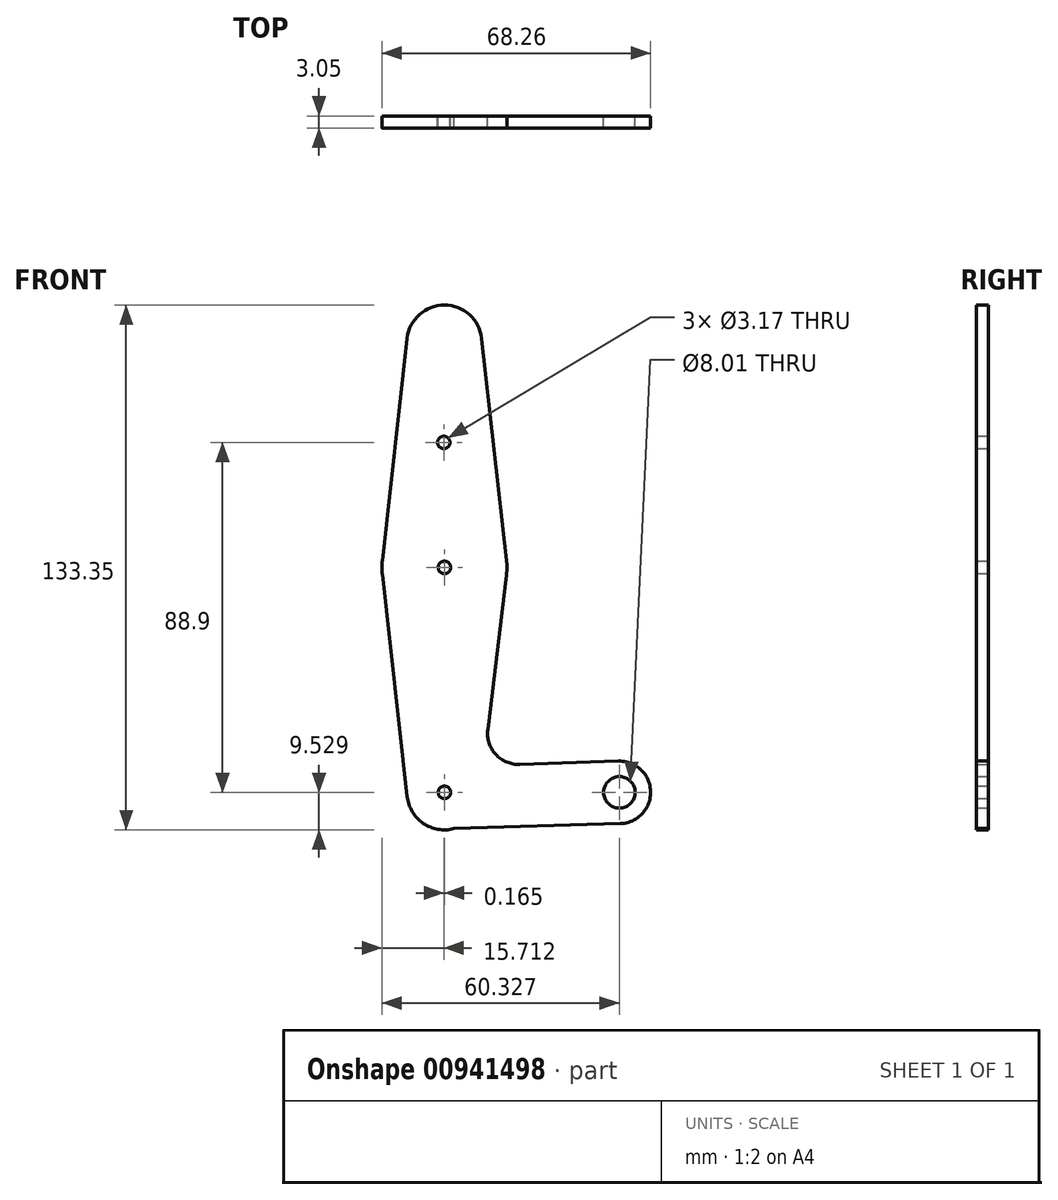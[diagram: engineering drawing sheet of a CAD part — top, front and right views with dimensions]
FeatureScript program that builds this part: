
annotation { "Feature Type Name" : "Feature", "Feature Type Description" : "" }
export const myFeature = defineFeature(function(context is Context, id is Id, definition is map)
    precondition{}
    {
        {
            var Q0;
            Q0=qCreatedBy(makeId("Front.planeOp"),FACE);
            var sketch = newSketch(context, id + "F0", { "sketchPlane" : qUnion([Q0])});
            skLineSegment(sketch, "E0", {"start": v(-39.9, 67.03) * mm, "end": v(-39.9, -47.27) * mm, "construction": true});
            skLineSegment(sketch, "E1", {"start": v(-39.9, -47.27) * mm, "end": v(4.56, -47.27) * mm, "construction": true});
            skCircle(sketch, "E2", {"center": v(-39.9, 67.03) * mm, "radius": 9.53 * mm});
            skCircle(sketch, "E3", {"center": v(-39.9, 9.88) * mm, "radius": 15.88 * mm});
            skCircle(sketch, "E4", {"center": v(-39.9, -47.27) * mm, "radius": 9.53 * mm});
            skCircle(sketch, "E5", {"center": v(4.56, -47.27) * mm, "radius": 7.94 * mm});
            skLineSegment(sketch, "E6", {"start": v(-30.43, 68.09) * mm, "end": v(-24.12, 11.64) * mm});
            skLineSegment(sketch, "E7", {"start": v(-49.36, 68.09) * mm, "end": v(-55.67, 11.64) * mm});
            skLineSegment(sketch, "E8", {"start": v(-55.67, 8.11) * mm, "end": v(-49.36, -48.33) * mm});
            skLineSegment(sketch, "E9", {"start": v(-28.88, -31.29) * mm, "end": v(-24.12, 8.1) * mm});
            skLineSegment(sketch, "E10", {"start": v(-20.71, -40.19) * mm, "end": v(4.56, -39.33) * mm});
            skCircle(sketch, "E11", {"center": v(-40.06, 41.63) * mm, "radius": 1.59 * mm});
            skCircle(sketch, "E12", {"center": v(-39.9, 9.88) * mm, "radius": 1.59 * mm});
            skCircle(sketch, "E13", {"center": v(-39.9, -47.27) * mm, "radius": 1.59 * mm});
            skCircle(sketch, "E14", {"center": v(4.56, -47.27) * mm, "radius": 4 * mm});
            skLineSegment(sketch, "E15", {"start": v(-41.75, -56.61) * mm, "end": v(4.8, -55.2) * mm});
            skPoint(sketch, "E16.newPointA", {"position": v(-30.94, -48.33) * mm});
            skPoint(sketch, "E16.newPointB", {"position": v(-39.9, -40.84) * mm});
            skArc(sketch, "E16.filletArc", {"start": v(-28.88, -31.29) * mm, "mid": v(-26.84, -37.61) * mm, "end": v(-20.71, -40.19) * mm});
            skSolve(sketch);
        }
        {
            var Q0;
            Q0 = qSketchRegion(id + "F0", true);
            extrude(context, id + "F1", {"entities" : qUnion([Q0]), "depth" : 3.05 * mm, "offsetDistance" : 25.4 * mm});
        }
    });
